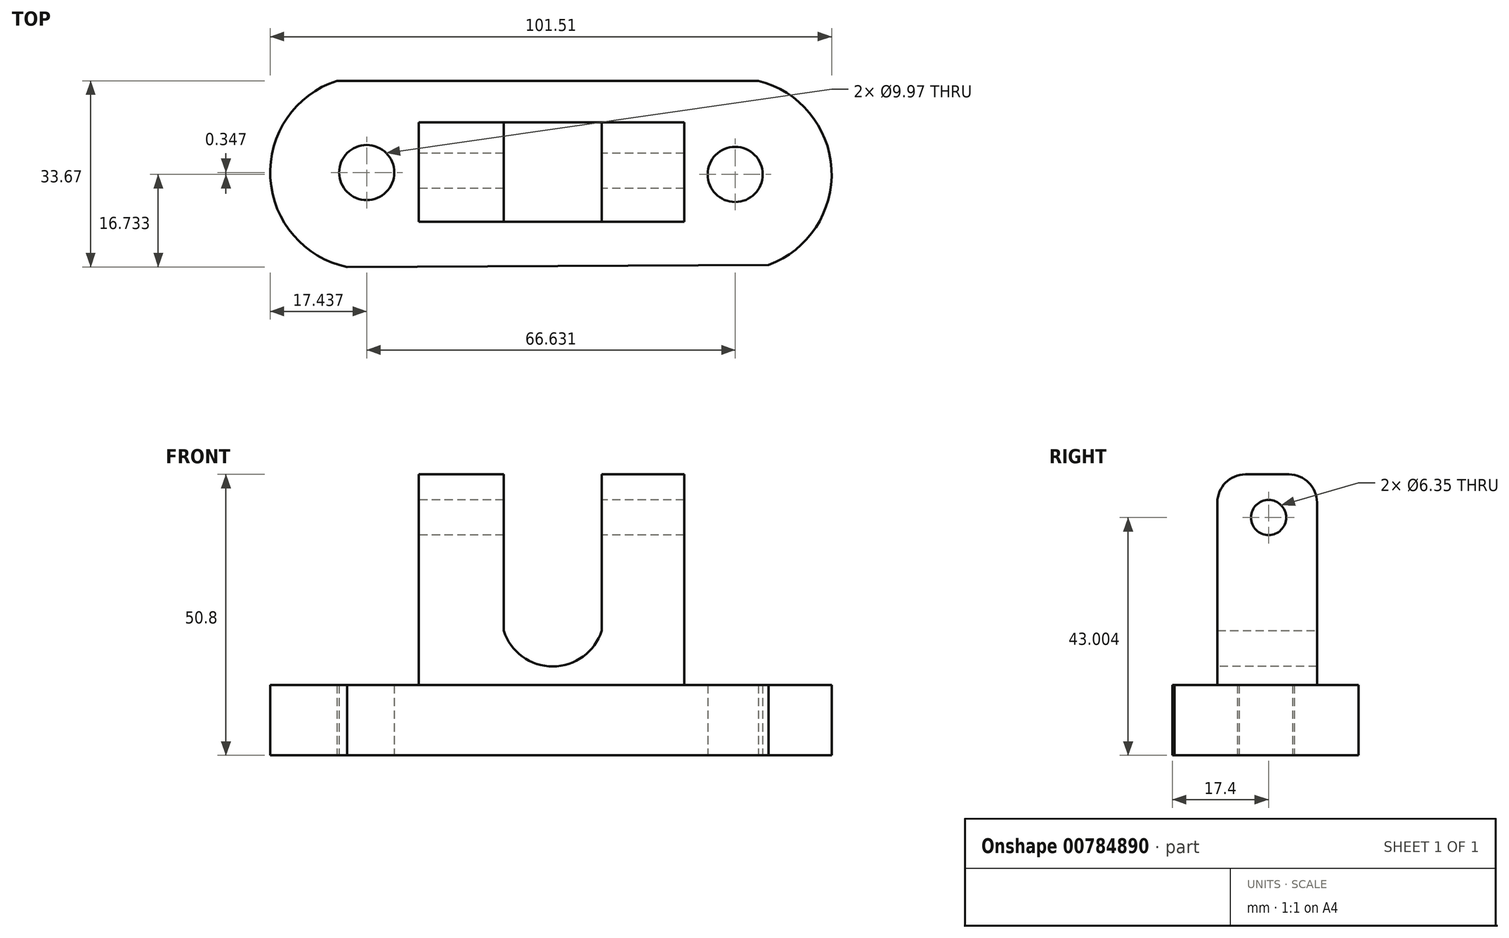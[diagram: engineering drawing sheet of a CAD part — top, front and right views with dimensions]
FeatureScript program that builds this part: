
annotation { "Feature Type Name" : "Feature", "Feature Type Description" : "" }
export const myFeature = defineFeature(function(context is Context, id is Id, definition is map)
    precondition{}
    {
        {
            var Q0;
            Q0=qCreatedBy(makeId("Top.planeOp"),FACE);
            var sketch = newSketch(context, id + "F0", { "sketchPlane" : qUnion([Q0])});
            skArc(sketch, "E0", {"start": v(-40.13, 16.27) * mm, "mid": v(-52.15, -1.29) * mm, "end": v(-38.26, -17.4) * mm});
            skArc(sketch, "E1", {"start": v(37.94, -17.03) * mm, "mid": v(49.31, 0.3) * mm, "end": v(36.07, 16.27) * mm});
            skLineSegment(sketch, "E2", {"start": v(-40.13, 16.27) * mm, "end": v(36.07, 16.27) * mm});
            skLineSegment(sketch, "E3", {"start": v(-38.26, -17.4) * mm, "end": v(37.94, -17.03) * mm});
            skCircle(sketch, "E4", {"center": v(-34.73, -0.32) * mm, "radius": 4.98 * mm});
            skCircle(sketch, "E5", {"center": v(31.9, -0.67) * mm, "radius": 4.98 * mm});
            skLineSegment(sketch, "E6.bottom", {"start": v(-25.3, 8.76) * mm, "end": v(-9.96, 8.76) * mm});
            skLineSegment(sketch, "E6.top", {"start": v(-25.3, -9.25) * mm, "end": v(-9.96, -9.25) * mm});
            skLineSegment(sketch, "E6.left", {"start": v(-25.3, 8.76) * mm, "end": v(-25.3, -9.25) * mm});
            skLineSegment(sketch, "E6.right", {"start": v(-9.96, 8.76) * mm, "end": v(-9.96, -9.25) * mm});
            skLineSegment(sketch, "E7.bottom", {"start": v(7.77, 8.76) * mm, "end": v(22.67, 8.76) * mm});
            skLineSegment(sketch, "E7.top", {"start": v(7.77, -9.25) * mm, "end": v(22.67, -9.25) * mm});
            skLineSegment(sketch, "E7.left", {"start": v(7.77, 8.76) * mm, "end": v(7.77, -9.25) * mm});
            skLineSegment(sketch, "E7.right", {"start": v(22.67, 8.76) * mm, "end": v(22.67, -9.25) * mm});
            skSolve(sketch);
        }
        {
            var Q0;
            Q0=makeQuery(id+"F0.imprint","IMPRINT",FACE,{"disambiguationData":[TD([[makeQuery(id+"F0.imprint","IMPRINT",EDGE,{"derivedFrom":sQuery(id+"F0.wireOp",EDGE,"E0")}),1.0]])]});
            var Q1;
            Q1=makeQuery(id+"F0.imprint","IMPRINT",FACE,{"disambiguationData":[TD([[makeQuery(id+"F0.imprint","IMPRINT",EDGE,{"derivedFrom":sQuery(id+"F0.wireOp",EDGE,"E6.bottom")}),-1.0]])]});
            var Q2;
            Q2=makeQuery(id+"F0.imprint","IMPRINT",FACE,{"disambiguationData":[TD([[makeQuery(id+"F0.imprint","IMPRINT",EDGE,{"derivedFrom":sQuery(id+"F0.wireOp",EDGE,"E7.bottom")}),-1.0]])]});
            extrude(context, id + "F1", {"entities" : qUnion([Q0, Q1, Q2]), "depth" : 12.7 * mm, "offsetDistance" : 25.4 * mm});
        }
        {
            var Q0;
            Q0=makeQuery(id+"F0.imprint","IMPRINT",FACE,{"disambiguationData":[TD([[makeQuery(id+"F0.imprint","IMPRINT",EDGE,{"derivedFrom":sQuery(id+"F0.wireOp",EDGE,"E6.bottom")}),-1.0]])]});
            var Q1;
            Q1=makeQuery(id+"F0.imprint","IMPRINT",FACE,{"disambiguationData":[TD([[makeQuery(id+"F0.imprint","IMPRINT",EDGE,{"derivedFrom":sQuery(id+"F0.wireOp",EDGE,"E7.bottom")}),-1.0]])]});
            extrude(context, id + "F2", {"entities" : qUnion([Q0, Q1]), "operationType" : NewBodyOperationType.ADD, "depth" : 50.8 * mm, "offsetDistance" : 25.4 * mm});
        }
        {
            var Q0;
            Q0=makeQuery(id+"F2.opExtrude","CAP_EDGE",EDGE,{"disambiguationData":[OSD([sQuery(id+"F0.wireOp",EDGE,"E6.top")])],"isStart":false});
            var Q1;
            Q1=makeQuery(id+"F2.opExtrude","CAP_EDGE",EDGE,{"disambiguationData":[OSD([sQuery(id+"F0.wireOp",EDGE,"E6.bottom")])],"isStart":false});
            var Q2;
            Q2=makeQuery(id+"F2.opExtrude","CAP_EDGE",EDGE,{"disambiguationData":[OSD([sQuery(id+"F0.wireOp",EDGE,"E7.bottom")])],"isStart":false});
            var Q3;
            Q3=makeQuery(id+"F2.opExtrude","CAP_EDGE",EDGE,{"disambiguationData":[OSD([sQuery(id+"F0.wireOp",EDGE,"E7.top")])],"isStart":false});
            fillet(context, id + "F3", {"entities" : qUnion([Q0, Q1, Q2, Q3]), "radius" : 5.08 * mm, "tangentPropagation" : true, "allowEdgeOverflow" : false});
        }
        {
            var Q0;
            Q0=makeQuery(id+"F2.opExtrude","SWEPT_FACE",FACE,{"disambiguationData":[OSD([sQuery(id+"F0.wireOp",EDGE,"E6.left")])]});
            var sketch = newSketch(context, id + "F4", { "sketchPlane" : qUnion([Q0])});
            skCircle(sketch, "E8", {"center": v(0, 43) * mm, "radius": 3.07 * mm});
            skSolve(sketch);
        }
        {
            var Q0;
            Q0=makeQuery(id+"F2.opExtrude","SWEPT_FACE",FACE,{"disambiguationData":[OSD([sQuery(id+"F0.wireOp",EDGE,"E6.right")])]});
            var sketch = newSketch(context, id + "F5", { "sketchPlane" : qUnion([Q0])});
            skLineSegment(sketch, "E9", {"start": v(-9.25, 22.54) * mm, "end": v(8.76, 22.54) * mm});
            skSolve(sketch);
        }
        {
            var Q0;
            Q0=sQuery(id+"F4.wireOp",VERTEX,"E8.center");
            var Q1;
            Q1=makeQuery(id+"F1.opExtrude","SWEPT_BODY",BODY,{"disambiguationData":[OSD([sQuery(id+"F0.wireOp",EDGE,"E0"),sQuery(id+"F0.wireOp",EDGE,"E1"),sQuery(id+"F0.wireOp",EDGE,"E2"),sQuery(id+"F0.wireOp",EDGE,"E3"),sQuery(id+"F0.wireOp",EDGE,"E4"),sQuery(id+"F0.wireOp",EDGE,"E5")])]});
            hole(context, id + "F6", {"style" : HoleStyle.SIMPLE, "endStyle" : HoleEndStyle.THROUGH, "holeDiameter" : 6.35 * mm, "majorDiameter" : 6.35 * mm, "isTappedThrough" : true, "tappedDepth" : 12.7 * mm, "tapClearance" : 3, "locations" : qUnion([Q0]), "scope" : qUnion([Q1])});
        }
        {
            var Q0;
            {var subQ0=sQuery(id+"F5.wireOp",EDGE,"E9");Q0=makeQuery(id+"F5.imprint","IMPRINT",FACE,{"disambiguationData":[TD([[makeQuery(id+"F5.imprint","IMPRINT",EDGE,{"derivedFrom":subQ0}),-1.0]])]});}
            extrude(context, id + "F7", {"entities" : qUnion([Q0]), "operationType" : NewBodyOperationType.ADD, "depth" : 17.78 * mm, "offsetDistance" : 25.4 * mm});
        }
        {
            var Q0;
            {var subQ0=sQuery(id+"F0.wireOp",EDGE,"E6.top");Q0=makeQuery(id+"F7.boolean.opBoolean","MERGE",FACE,{"derivedFrom":[makeQuery(id+"F2.opExtrude","SWEPT_FACE",FACE,{"disambiguationData":[OSD([subQ0])]}),makeQuery(id+"F2.opExtrude","SWEPT_FACE",FACE,{"disambiguationData":[OSD([sQuery(id+"F0.wireOp",EDGE,"E7.top")])]}),makeQuery(id+"F7.opExtrude","SWEPT_FACE",FACE,{"disambiguationData":[OSD([subQ0,sQuery(id+"F0.wireOp",EDGE,"E6.right")])]})]});}
            var sketch = newSketch(context, id + "F8", { "sketchPlane" : qUnion([Q0])});
            skArc(sketch, "E10", {"start": v(-9.96, 22.54) * mm, "mid": v(-1.1, 16.07) * mm, "end": v(7.77, 22.54) * mm});
            skSolve(sketch);
        }
        {
            var Q0;
            Q0=makeQuery(id+"F8.imprint","IMPRINT",FACE,{"disambiguationData":[TD([[makeQuery(id+"F8.imprint","IMPRINT",EDGE,{"derivedFrom":sQuery(id+"F8.wireOp",EDGE,"E10")}),1.0]])]});
            extrude(context, id + "F9", {"entities" : qUnion([Q0]), "operationType" : NewBodyOperationType.REMOVE, "oppositeDirection" : true, "depth" : 25.4 * mm, "offsetDistance" : 25.4 * mm});
        }
    });
